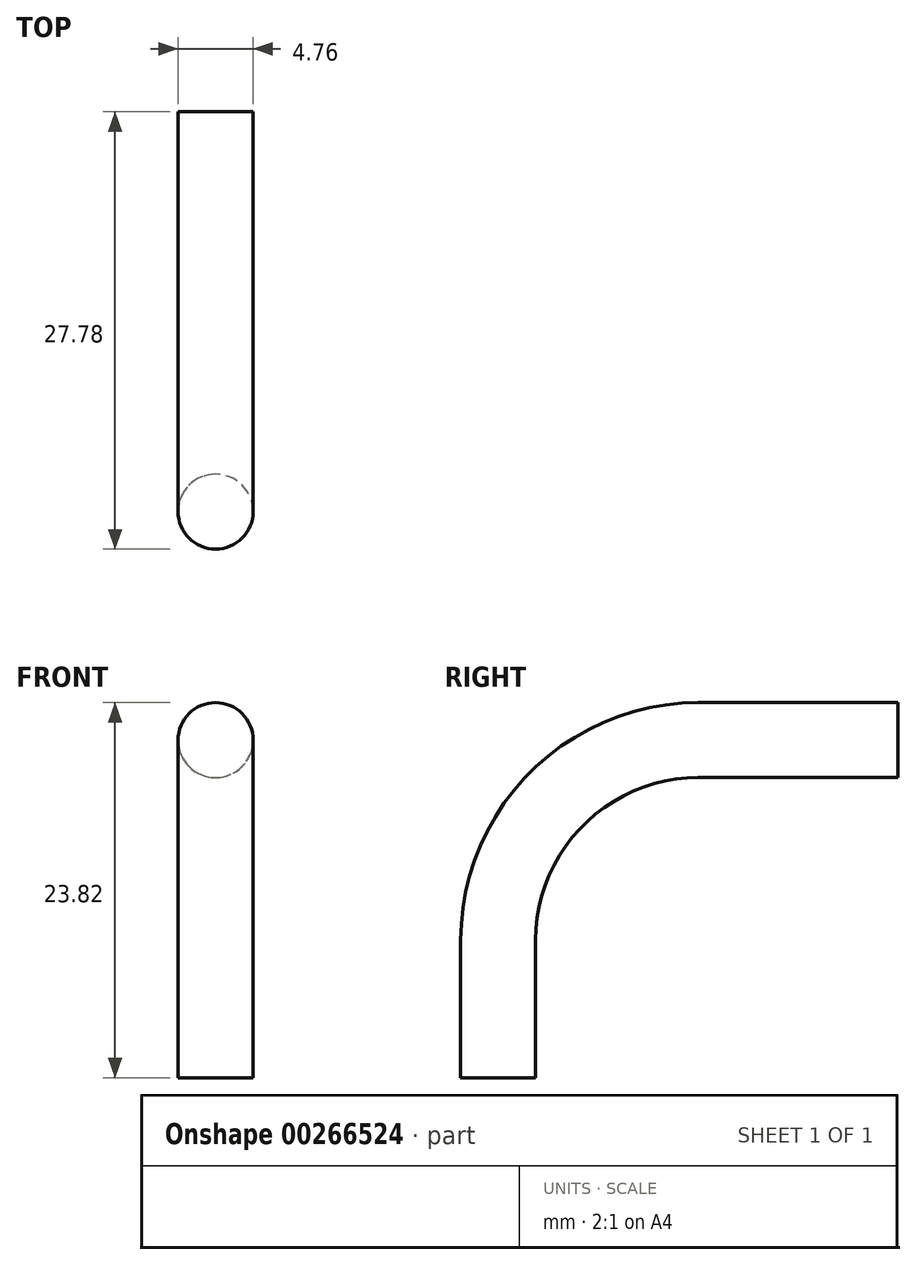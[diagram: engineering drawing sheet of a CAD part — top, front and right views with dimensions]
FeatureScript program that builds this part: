
annotation { "Feature Type Name" : "Feature", "Feature Type Description" : "" }
export const myFeature = defineFeature(function(context is Context, id is Id, definition is map)
    precondition{}
    {
        {
            var Q0;
            Q0=qCreatedBy(makeId("Front.planeOp"),FACE);
            var sketch = newSketch(context, id + "F0", { "sketchPlane" : qUnion([Q0])});
            skCircle(sketch, "E0", {"center": v(0, 0) * mm, "radius": 2.38 * mm});
            skLineSegment(sketch, "E1", {"start": v(-12.72, -12.7) * mm, "end": v(14.88, -12.7) * mm});
            skSolve(sketch);
        }
        {
            var Q0;
            Q0=makeQuery(id+"F0.imprint","IMPRINT",FACE,{"disambiguationData":[TD([[makeQuery(id+"F0.imprint","IMPRINT",EDGE,{"derivedFrom":sQuery(id+"F0.wireOp",EDGE,"E0")}),1.0]])]});
            var Q1;
            Q1=sQuery(id+"F0.wireOp",EDGE,"E1");
            revolve(context, id + "F1", {"entities" : qUnion([Q0]), "axis" : qUnion([Q1]), "revolveType" : RevolveType.ONE_DIRECTION, "angle" : 90 * degree});
        }
        {
            var Q0;
            Q0=makeQuery(id+"F1.opRevolve","CAP_FACE",FACE,{"disambiguationData":[OSD([sQuery(id+"F0.wireOp",EDGE,"E0")])],"isStart":false});
            extrude(context, id + "F2", {"entities" : qUnion([Q0]), "operationType" : NewBodyOperationType.ADD, "depth" : 8.74 * mm});
        }
        {
            var Q0;
            Q0=makeQuery(id+"F1.opRevolve","CAP_FACE",FACE,{"disambiguationData":[OSD([sQuery(id+"F0.wireOp",EDGE,"E0")])],"isStart":true});
            extrude(context, id + "F3", {"entities" : qUnion([Q0]), "operationType" : NewBodyOperationType.ADD, "depth" : 12.7 * mm});
        }
    });
